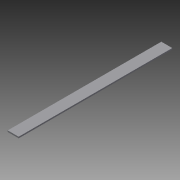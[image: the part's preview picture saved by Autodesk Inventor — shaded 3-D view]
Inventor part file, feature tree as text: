
AUTODESK INVENTOR PART (.ipt)
format: ipt  version: 2015 (Build 190159000, 159)  size: 67,584 bytes
history: native  units: in
note: dims shown in document units (in); Inventor stores cm internally (conversion verified against a paired STEP export)
features: extrude x1, sketch x1
ambient origin geometry x8: Origin, YZ Plane, XZ Plane, XY Plane, X Axis, Y Axis, Z Axis, Center Point
bodies: Solid1 (feature_tree)
feature tree (2):
  extrude  "Extrusion1"  Depth=0.125in
  sketch  "Sketch1"  dims[d0=1.0in d1=0.125in d2=14.0in d3=0.0in]
